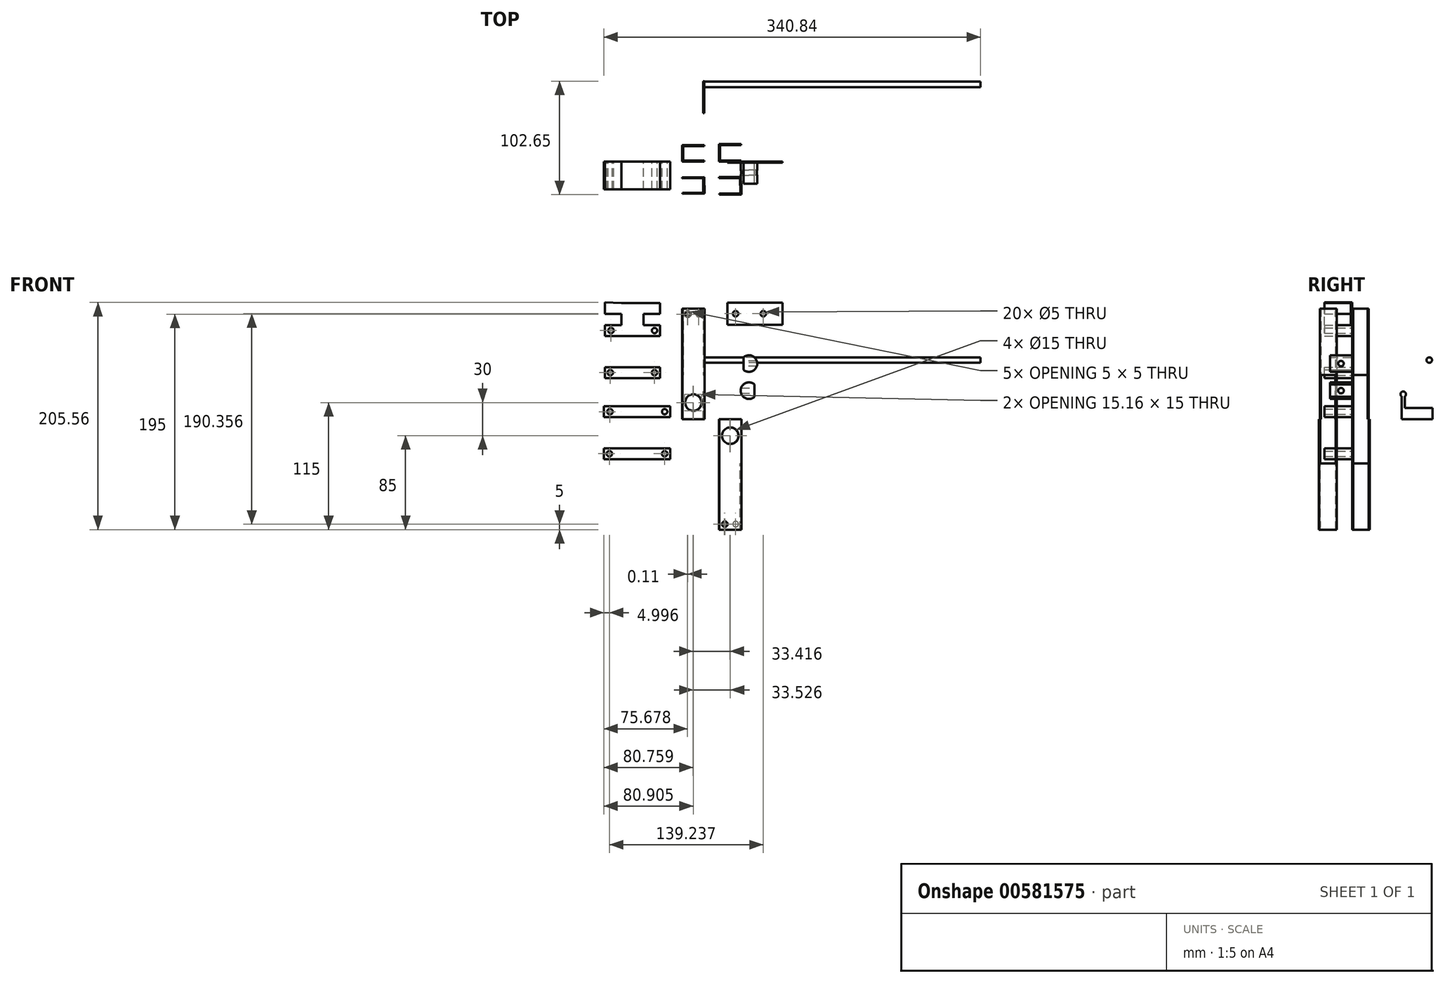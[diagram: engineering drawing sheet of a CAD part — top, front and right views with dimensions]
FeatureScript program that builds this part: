
annotation { "Feature Type Name" : "Feature", "Feature Type Description" : "" }
export const myFeature = defineFeature(function(context is Context, id is Id, definition is map)
    precondition{}
    {
        {
            var Q0;
            Q0=qCreatedBy(makeId("Top.planeOp"),FACE);
            var sketch = newSketch(context, id + "F0", { "sketchPlane" : qUnion([Q0])});
            skLineSegment(sketch, "E0", {"start": v(0, 15) * mm, "end": v(-20, 15) * mm});
            skLineSegment(sketch, "E1", {"start": v(-20, 15) * mm, "end": v(-20, 0) * mm});
            skLineSegment(sketch, "E2", {"start": v(-20, 0) * mm, "end": v(0, 0) * mm});
            skLineSegment(sketch, "E3", {"start": v(0, 0) * mm, "end": v(0, 1) * mm});
            skLineSegment(sketch, "E4", {"start": v(0, 1) * mm, "end": v(-19, 1) * mm});
            skLineSegment(sketch, "E5", {"start": v(-19, 1) * mm, "end": v(-19, 14) * mm});
            skLineSegment(sketch, "E6", {"start": v(-19, 14) * mm, "end": v(0, 14) * mm});
            skLineSegment(sketch, "E7", {"start": v(0, 14) * mm, "end": v(0, 15) * mm});
            skLineSegment(sketch, "E8", {"start": v(33.42, 1) * mm, "end": v(14.42, 1) * mm});
            skLineSegment(sketch, "E9", {"start": v(14.42, 1) * mm, "end": v(14.42, 15) * mm});
            skLineSegment(sketch, "E10", {"start": v(14.42, 15) * mm, "end": v(33.42, 15) * mm});
            skLineSegment(sketch, "E11", {"start": v(33.42, 15) * mm, "end": v(33.42, 16) * mm});
            skLineSegment(sketch, "E12", {"start": v(33.42, 16) * mm, "end": v(13.42, 16) * mm});
            skLineSegment(sketch, "E13", {"start": v(13.42, 16) * mm, "end": v(13.42, 0) * mm});
            skLineSegment(sketch, "E14", {"start": v(13.42, 0) * mm, "end": v(33.42, 0) * mm});
            skLineSegment(sketch, "E15", {"start": v(33.42, 0) * mm, "end": v(33.42, 1) * mm});
            skLineSegment(sketch, "E16", {"start": v(-36.62, -7.13) * mm, "end": v(38.64, -6.85) * mm, "construction": true});
            skLineSegment(sketch, "E17.MirrorCS", {"start": v(-19, 16) * mm, "end": v(0, 16) * mm});
            skLineSegment(sketch, "E18.MirrorCS", {"start": v(-19.95, -14.13) * mm, "end": v(0.05, -13.99) * mm});
            skLineSegment(sketch, "E19.MirrorCS", {"start": v(0.16, -28.99) * mm, "end": v(-19.84, -29.13) * mm});
            skLineSegment(sketch, "E20.MirrorCS", {"start": v(13.47, -13.89) * mm, "end": v(33.47, -13.74) * mm});
            skLineSegment(sketch, "E21.MirrorCS", {"start": v(33.58, -29.74) * mm, "end": v(13.58, -29.89) * mm});
            skLineSegment(sketch, "E22", {"start": v(13.47, -13.89) * mm, "end": v(13.47, -14.89) * mm});
            skLineSegment(sketch, "E23", {"start": v(13.47, -14.89) * mm, "end": v(32.47, -14.75) * mm});
            skLineSegment(sketch, "E24", {"start": v(32.58, -28.75) * mm, "end": v(13.58, -28.89) * mm});
            skLineSegment(sketch, "E25", {"start": v(13.58, -28.89) * mm, "end": v(13.58, -29.89) * mm});
            skLineSegment(sketch, "E26", {"start": v(32.58, -28.75) * mm, "end": v(32.47, -14.75) * mm});
            skLineSegment(sketch, "E27", {"start": v(33.47, -13.74) * mm, "end": v(33.58, -29.74) * mm});
            skLineSegment(sketch, "E28", {"start": v(0.05, -13.99) * mm, "end": v(0.16, -28.99) * mm});
            skLineSegment(sketch, "E29", {"start": v(-19.95, -14.13) * mm, "end": v(-19.94, -15.13) * mm});
            skLineSegment(sketch, "E30", {"start": v(-19.94, -15.13) * mm, "end": v(-0.94, -15) * mm});
            skLineSegment(sketch, "E31", {"start": v(-0.94, -15) * mm, "end": v(-0.85, -28) * mm});
            skLineSegment(sketch, "E32", {"start": v(-0.85, -28) * mm, "end": v(-19.84, -28.13) * mm});
            skLineSegment(sketch, "E33", {"start": v(-19.84, -29.13) * mm, "end": v(-19.84, -28.13) * mm});
            skSolve(sketch);
        }
        {
            var Q0;
            Q0=makeQuery(id+"F0.imprint","IMPRINT",FACE,{"disambiguationData":[TD([[makeQuery(id+"F0.imprint","IMPRINT",EDGE,{"derivedFrom":sQuery(id+"F0.wireOp",EDGE,"E0")}),1.0]])]});
            var Q1;
            Q1=makeQuery(id+"F0.imprint","IMPRINT",FACE,{"disambiguationData":[TD([[makeQuery(id+"F0.imprint","IMPRINT",EDGE,{"derivedFrom":sQuery(id+"F0.wireOp",EDGE,"E19.MirrorCS")}),-1.0]])]});
            extrude(context, id + "F1", {"entities" : qUnion([Q0, Q1]), "depth" : 100 * mm, "offsetDistance" : 25 * mm});
        }
        {
            var Q0;
            Q0=makeQuery(id+"F1.opExtrude","SWEPT_FACE",FACE,{"disambiguationData":[OSD([sQuery(id+"F0.wireOp",EDGE,"E2")])]});
            var sketch = newSketch(context, id + "F2", { "sketchPlane" : qUnion([Q0])});
            skCircle(sketch, "E34", {"center": v(-10, 15) * mm, "radius": 7.5 * mm});
            skPoint(sketch, "E34.centerSnap0", {"position": v(-10, 0) * mm});
            skCircle(sketch, "E35", {"center": v(-5, 95) * mm, "radius": 2.5 * mm});
            skSolve(sketch);
        }
        {
            var Q0;
            Q0=makeQuery(id+"F2.imprint","IMPRINT",FACE,{"disambiguationData":[TD([[makeQuery(id+"F2.imprint","IMPRINT",EDGE,{"derivedFrom":sQuery(id+"F2.wireOp",EDGE,"E34")}),1.0]])]});
            var Q1;
            Q1=makeQuery(id+"F2.imprint","IMPRINT",FACE,{"disambiguationData":[TD([[makeQuery(id+"F2.imprint","IMPRINT",EDGE,{"derivedFrom":sQuery(id+"F2.wireOp",EDGE,"E35")}),1.0]])]});
            extrude(context, id + "F3", {"entities" : qUnion([Q0, Q1]), "operationType" : NewBodyOperationType.REMOVE, "endBound" : BoundingType.THROUGH_ALL, "oppositeDirection" : true, "depth" : 25 * mm, "offsetDistance" : 25 * mm});
        }
        {
            var Q0;
            Q0=makeQuery(id+"F1.opExtrude","SWEPT_FACE",FACE,{"disambiguationData":[OSD([sQuery(id+"F0.wireOp",EDGE,"E1")])]});
            var sketch = newSketch(context, id + "F4", { "sketchPlane" : qUnion([Q0])});
            skPoint(sketch, "E36.centerSnap0", {"position": v(-7.5, 0) * mm});
            skLineSegment(sketch, "E37", {"start": v(-14, 0) * mm, "end": v(-14, 40) * mm});
            skLineSegment(sketch, "E38", {"start": v(-14, 40) * mm, "end": v(-1, 40) * mm});
            skLineSegment(sketch, "E39", {"start": v(-1, 40) * mm, "end": v(-1, 0) * mm});
            skSolve(sketch);
        }
        {
            var Q0;
            {var subQ0=sQuery(id+"F4.wireOp",EDGE,"E37");Q0=makeQuery(id+"F4.imprint","IMPRINT",FACE,{"disambiguationData":[TD([[makeQuery(id+"F4.imprint","IMPRINT",EDGE,{"derivedFrom":subQ0}),-1.0]])]});}
            extrude(context, id + "F5", {"entities" : qUnion([Q0]), "operationType" : NewBodyOperationType.REMOVE, "endBound" : BoundingType.THROUGH_ALL, "oppositeDirection" : true, "depth" : 25 * mm, "offsetDistance" : 25 * mm});
        }
        {
            var Q0;
            Q0=makeQuery(id+"F0.imprint","IMPRINT",FACE,{"disambiguationData":[TD([[makeQuery(id+"F0.imprint","IMPRINT",EDGE,{"derivedFrom":sQuery(id+"F0.wireOp",EDGE,"E8")}),1.0]])]});
            var Q1;
            Q1=makeQuery(id+"F0.imprint","IMPRINT",FACE,{"disambiguationData":[TD([[makeQuery(id+"F0.imprint","IMPRINT",EDGE,{"derivedFrom":sQuery(id+"F0.wireOp",EDGE,"E20.MirrorCS")}),-1.0]])]});
            extrude(context, id + "F6", {"entities" : qUnion([Q0, Q1]), "oppositeDirection" : true, "depth" : 100 * mm, "offsetDistance" : 25 * mm});
        }
        {
            var Q0;
            Q0=makeQuery(id+"F6.opExtrude","SWEPT_FACE",FACE,{"disambiguationData":[OSD([sQuery(id+"F0.wireOp",EDGE,"E14")])]});
            var sketch = newSketch(context, id + "F7", { "sketchPlane" : qUnion([Q0])});
            skCircle(sketch, "E40", {"center": v(23.42, -15) * mm, "radius": 7.5 * mm});
            skPoint(sketch, "E40.centerSnap0", {"position": v(23.42, 0) * mm});
            skCircle(sketch, "E41", {"center": v(28.42, -95) * mm, "radius": 2.5 * mm});
            skSolve(sketch);
        }
        {
            var Q0;
            Q0=makeQuery(id+"F7.imprint","IMPRINT",FACE,{"disambiguationData":[TD([[makeQuery(id+"F7.imprint","IMPRINT",EDGE,{"derivedFrom":sQuery(id+"F7.wireOp",EDGE,"E40")}),1.0]])]});
            var Q1;
            Q1=makeQuery(id+"F7.imprint","IMPRINT",FACE,{"disambiguationData":[TD([[makeQuery(id+"F7.imprint","IMPRINT",EDGE,{"derivedFrom":sQuery(id+"F7.wireOp",EDGE,"E41")}),1.0]])]});
            extrude(context, id + "F8", {"entities" : qUnion([Q0, Q1]), "operationType" : NewBodyOperationType.REMOVE, "endBound" : BoundingType.THROUGH_ALL, "oppositeDirection" : true, "depth" : 25 * mm, "offsetDistance" : 25 * mm});
        }
        {
            var Q0;
            Q0=makeQuery(id+"F6.opExtrude","SWEPT_FACE",FACE,{"disambiguationData":[OSD([sQuery(id+"F0.wireOp",EDGE,"E13")])]});
            var sketch = newSketch(context, id + "F9", { "sketchPlane" : qUnion([Q0])});
            skLineSegment(sketch, "E42", {"start": v(-15, 0) * mm, "end": v(-15, -40) * mm});
            skLineSegment(sketch, "E43", {"start": v(-15, -40) * mm, "end": v(-1, -40) * mm});
            skLineSegment(sketch, "E44", {"start": v(-1, -40) * mm, "end": v(-1, 0) * mm});
            skSolve(sketch);
        }
        {
            var Q0;
            {var subQ0=sQuery(id+"F9.wireOp",EDGE,"E42");Q0=makeQuery(id+"F9.imprint","IMPRINT",FACE,{"disambiguationData":[TD([[makeQuery(id+"F9.imprint","IMPRINT",EDGE,{"derivedFrom":subQ0}),1.0]])]});}
            extrude(context, id + "F10", {"entities" : qUnion([Q0]), "operationType" : NewBodyOperationType.REMOVE, "endBound" : BoundingType.THROUGH_ALL, "oppositeDirection" : true, "depth" : 25 * mm, "offsetDistance" : 25 * mm});
        }
        {
            var Q0;
            Q0=qCreatedBy(makeId("Front.planeOp"),FACE);
            var sketch = newSketch(context, id + "F11", { "sketchPlane" : qUnion([Q0])});
            skLineSegment(sketch, "E45.bottom", {"start": v(20.9, 105.36) * mm, "end": v(70.9, 105.36) * mm});
            skLineSegment(sketch, "E45.top", {"start": v(20.9, 85.36) * mm, "end": v(70.9, 85.36) * mm});
            skLineSegment(sketch, "E45.left", {"start": v(20.9, 105.36) * mm, "end": v(20.9, 85.36) * mm});
            skLineSegment(sketch, "E45.right", {"start": v(70.9, 105.36) * mm, "end": v(70.9, 85.36) * mm});
            skCircle(sketch, "E46", {"center": v(28.4, 95.36) * mm, "radius": 2.5 * mm});
            skPoint(sketch, "E46.centerSnap0", {"position": v(20.9, 95.36) * mm});
            skCircle(sketch, "E47.MirrorC", {"center": v(53.4, 95.36) * mm, "radius": 2.5 * mm});
            skSolve(sketch);
        }
        {
            var Q0;
            Q0=makeQuery(id+"F11.imprint","IMPRINT",FACE,{"disambiguationData":[TD([[makeQuery(id+"F11.imprint","IMPRINT",EDGE,{"derivedFrom":sQuery(id+"F11.wireOp",EDGE,"E45.bottom")}),-1.0]])]});
            extrude(context, id + "F12", {"entities" : qUnion([Q0]), "depth" : 1 * mm, "offsetDistance" : 25 * mm});
        }
        {
            var Q0;
            Q0=makeQuery(id+"F1.opExtrude","SWEPT_FACE",FACE,{"disambiguationData":[OSD([sQuery(id+"F0.wireOp",EDGE,"E19.MirrorCS")])]});
            var sketch = newSketch(context, id + "F13", { "sketchPlane" : qUnion([Q0])});
            skCircle(sketch, "E48", {"center": v(-15.05, 95) * mm, "radius": 2.5 * mm});
            skCircle(sketch, "E49", {"center": v(-10.05, 15) * mm, "radius": 7.5 * mm});
            skPoint(sketch, "E49.centerSnap0", {"position": v(-10.05, 0) * mm});
            skSolve(sketch);
        }
        {
            var Q0;
            Q0=makeQuery(id+"F13.imprint","IMPRINT",FACE,{"disambiguationData":[TD([[makeQuery(id+"F13.imprint","IMPRINT",EDGE,{"derivedFrom":sQuery(id+"F13.wireOp",EDGE,"E48")}),1.0]])]});
            var Q1;
            Q1=makeQuery(id+"F13.imprint","IMPRINT",FACE,{"disambiguationData":[TD([[makeQuery(id+"F13.imprint","IMPRINT",EDGE,{"derivedFrom":sQuery(id+"F13.wireOp",EDGE,"E49")}),1.0]])]});
            extrude(context, id + "F14", {"entities" : qUnion([Q0, Q1]), "operationType" : NewBodyOperationType.REMOVE, "endBound" : BoundingType.THROUGH_ALL, "oppositeDirection" : true, "depth" : 25 * mm, "offsetDistance" : 25 * mm});
        }
        {
            var Q0;
            Q0=makeQuery(id+"F6.opExtrude","SWEPT_FACE",FACE,{"disambiguationData":[OSD([sQuery(id+"F0.wireOp",EDGE,"E21.MirrorCS")])]});
            var sketch = newSketch(context, id + "F15", { "sketchPlane" : qUnion([Q0])});
            skCircle(sketch, "E50", {"center": v(23.36, -15) * mm, "radius": 7.5 * mm});
            skPoint(sketch, "E50.centerSnap0", {"position": v(23.36, 0) * mm});
            skCircle(sketch, "E51", {"center": v(18.36, -95) * mm, "radius": 2.5 * mm});
            skSolve(sketch);
        }
        {
            var Q0;
            Q0 = qSketchRegion(id + "F15", true);
            extrude(context, id + "F16", {"entities" : qUnion([Q0]), "operationType" : NewBodyOperationType.REMOVE, "endBound" : BoundingType.THROUGH_ALL, "oppositeDirection" : true, "depth" : 25 * mm, "offsetDistance" : 25 * mm});
        }
        {
            var Q0;
            Q0=makeQuery(id+"F6.opExtrude","SWEPT_FACE",FACE,{"disambiguationData":[OSD([sQuery(id+"F0.wireOp",EDGE,"E27")])]});
            var sketch = newSketch(context, id + "F17", { "sketchPlane" : qUnion([Q0])});
            skLineSegment(sketch, "E52", {"start": v(-14.99, -40) * mm, "end": v(-28.99, -40) * mm});
            skLineSegment(sketch, "E53", {"start": v(-28.99, -40) * mm, "end": v(-28.99, 0) * mm});
            skLineSegment(sketch, "E54", {"start": v(-14.99, -40) * mm, "end": v(-14.99, 0) * mm});
            skSolve(sketch);
        }
        {
            var Q0;
            Q0=makeQuery(id+"F17.imprint","IMPRINT",FACE,{"disambiguationData":[TD([[makeQuery(id+"F17.imprint","IMPRINT",EDGE,{"derivedFrom":sQuery(id+"F17.wireOp",EDGE,"E52")}),-1.0]])]});
            extrude(context, id + "F18", {"entities" : qUnion([Q0]), "operationType" : NewBodyOperationType.REMOVE, "endBound" : BoundingType.THROUGH_ALL, "oppositeDirection" : true, "depth" : 25 * mm, "offsetDistance" : 25 * mm});
        }
        {
            var Q0;
            Q0=makeQuery(id+"F1.opExtrude","SWEPT_FACE",FACE,{"disambiguationData":[OSD([sQuery(id+"F0.wireOp",EDGE,"E28")])]});
            var sketch = newSketch(context, id + "F19", { "sketchPlane" : qUnion([Q0])});
            skLineSegment(sketch, "E55", {"start": v(-14.99, 0) * mm, "end": v(-14.99, 40) * mm});
            skLineSegment(sketch, "E56", {"start": v(-14.99, 40) * mm, "end": v(-27.99, 40) * mm});
            skLineSegment(sketch, "E57", {"start": v(-27.99, 40) * mm, "end": v(-27.99, 0) * mm});
            skSolve(sketch);
        }
        {
            var Q0;
            {var subQ0=sQuery(id+"F19.wireOp",EDGE,"E55");Q0=makeQuery(id+"F19.imprint","IMPRINT",FACE,{"disambiguationData":[TD([[makeQuery(id+"F19.imprint","IMPRINT",EDGE,{"derivedFrom":subQ0}),1.0]])]});}
            extrude(context, id + "F20", {"entities" : qUnion([Q0]), "operationType" : NewBodyOperationType.REMOVE, "oppositeDirection" : true, "depth" : 25 * mm, "offsetDistance" : 25 * mm});
        }
        {
            var Q0;
            Q0=qCreatedBy(makeId("Front.planeOp"),FACE);
            var sketch = newSketch(context, id + "F21", { "sketchPlane" : qUnion([Q0])});
            skArc(sketch, "E58", {"start": v(35.49, 44.6) * mm, "mid": v(47.93, 50.24) * mm, "end": v(35.49, 55.88) * mm});
            skArc(sketch, "E59", {"start": v(45.38, 31.4) * mm, "mid": v(32.93, 25.77) * mm, "end": v(45.38, 20.13) * mm});
            skLineSegment(sketch, "E60", {"start": v(35.49, 55.88) * mm, "end": v(35.49, 44.6) * mm});
            skLineSegment(sketch, "E61.trimOffspring", {"start": v(45.38, 31.4) * mm, "end": v(45.38, 20.13) * mm});
            skPoint(sketch, "E62.orphan", {"position": v(40.43, 57.74) * mm});
            skSolve(sketch);
        }
        {
            var Q0;
            Q0=makeQuery(id+"F21.imprint","IMPRINT",FACE,{"disambiguationData":[TD([[makeQuery(id+"F21.imprint","IMPRINT",EDGE,{"derivedFrom":sQuery(id+"F21.wireOp",EDGE,"E58")}),1.0]])]});
            var Q1;
            Q1=makeQuery(id+"F21.imprint","IMPRINT",FACE,{"disambiguationData":[TD([[makeQuery(id+"F21.imprint","IMPRINT",EDGE,{"derivedFrom":sQuery(id+"F21.wireOp",EDGE,"E59")}),1.0]])]});
            extrude(context, id + "F22", {"entities" : qUnion([Q0, Q1]), "depth" : 20 * mm, "offsetDistance" : 25 * mm});
        }
        {
            var Q0;
            Q0=qCreatedBy(makeId("Right.planeOp"),FACE);
            var sketch = newSketch(context, id + "F23", { "sketchPlane" : qUnion([Q0])});
            skCircle(sketch, "E63", {"center": v(69.88, 53.43) * mm, "radius": 2.5 * mm});
            skSolve(sketch);
        }
        {
            var Q0;
            Q0=makeQuery(id+"F23.imprint","IMPRINT",FACE,{"disambiguationData":[TD([[makeQuery(id+"F23.imprint","IMPRINT",EDGE,{"derivedFrom":sQuery(id+"F23.wireOp",EDGE,"E63")}),1.0]])]});
            extrude(context, id + "F24", {"entities" : qUnion([Q0]), "depth" : 250 * mm, "offsetDistance" : 25 * mm});
        }
        {
            var Q0;
            Q0=qCreatedBy(makeId("Front.planeOp"),FACE);
            var sketch = newSketch(context, id + "F25", { "sketchPlane" : qUnion([Q0])});
            skLineSegment(sketch, "E64.top", {"start": v(-89.95, 75.12) * mm, "end": v(-39.95, 75.12) * mm});
            skLineSegment(sketch, "E64.left", {"start": v(-89.95, 85.12) * mm, "end": v(-89.95, 75.12) * mm});
            skLineSegment(sketch, "E64.right", {"start": v(-39.95, 85.12) * mm, "end": v(-39.95, 75.12) * mm});
            skCircle(sketch, "E65", {"center": v(-84.38, 80.12) * mm, "radius": 2.5 * mm});
            skPoint(sketch, "E65.centerSnap0", {"position": v(-89.95, 80.12) * mm});
            skCircle(sketch, "E66", {"center": v(-44.95, 80.12) * mm, "radius": 2.41 * mm});
            skPoint(sketch, "E66.centerSnap0", {"position": v(-39.95, 80.12) * mm});
            skLineSegment(sketch, "E67.MirrorCS", {"start": v(-89.95, 47.06) * mm, "end": v(-39.95, 47.06) * mm});
            skLineSegment(sketch, "E68.MirrorCS", {"start": v(-89.95, 37.06) * mm, "end": v(-89.95, 47.06) * mm});
            skLineSegment(sketch, "E69.MirrorCS", {"start": v(-89.95, 37.06) * mm, "end": v(-39.95, 37.06) * mm});
            skLineSegment(sketch, "E70.MirrorCS", {"start": v(-39.95, 37.06) * mm, "end": v(-39.95, 47.06) * mm});
            skCircle(sketch, "E71", {"center": v(-84.95, 42.06) * mm, "radius": 2.5 * mm});
            skPoint(sketch, "E71.centerSnap0", {"position": v(-89.95, 42.06) * mm});
            skCircle(sketch, "E72", {"center": v(-44.95, 42.06) * mm, "radius": 2.5 * mm});
            skPoint(sketch, "E72.centerSnap0", {"position": v(-39.95, 42.06) * mm});
            skLineSegment(sketch, "E73.bottom", {"start": v(-90.84, 11.74) * mm, "end": v(-30.84, 11.74) * mm});
            skLineSegment(sketch, "E73.top", {"start": v(-90.84, 1.74) * mm, "end": v(-30.84, 1.74) * mm});
            skLineSegment(sketch, "E73.left", {"start": v(-90.84, 11.74) * mm, "end": v(-90.84, 1.74) * mm});
            skLineSegment(sketch, "E73.right", {"start": v(-30.84, 11.74) * mm, "end": v(-30.84, 1.74) * mm});
            skCircle(sketch, "E74", {"center": v(-85.27, 6.74) * mm, "radius": 2.5 * mm});
            skPoint(sketch, "E74.centerSnap0", {"position": v(-90.84, 6.74) * mm});
            skCircle(sketch, "E75", {"center": v(-35.84, 6.74) * mm, "radius": 2.41 * mm});
            skPoint(sketch, "E75.centerSnap0", {"position": v(-30.84, 6.74) * mm});
            skLineSegment(sketch, "E76.MirrorCS", {"start": v(-90.84, -36.32) * mm, "end": v(-90.84, -26.32) * mm});
            skLineSegment(sketch, "E77.MirrorCS", {"start": v(-30.84, -36.32) * mm, "end": v(-30.84, -26.32) * mm});
            skCircle(sketch, "E78", {"center": v(-85.84, -31.32) * mm, "radius": 2.5 * mm});
            skPoint(sketch, "E78.centerSnap0", {"position": v(-90.84, -31.32) * mm});
            skCircle(sketch, "E79", {"center": v(-35.84, -31.32) * mm, "radius": 2.5 * mm});
            skPoint(sketch, "E79.centerSnap0", {"position": v(-30.84, -31.32) * mm});
            skLineSegment(sketch, "E80", {"start": v(-90.84, -26.32) * mm, "end": v(-30.84, -26.32) * mm});
            skLineSegment(sketch, "E81", {"start": v(-90.84, -36.32) * mm, "end": v(-30.84, -36.32) * mm});
            skLineSegment(sketch, "E82", {"start": v(-74.95, 85.12) * mm, "end": v(-74.95, 95.12) * mm});
            skLineSegment(sketch, "E83", {"start": v(-74.95, 105.12) * mm, "end": v(-64.95, 105.12) * mm});
            skLineSegment(sketch, "E84.MirrorCS", {"start": v(-54.95, 85.12) * mm, "end": v(-54.95, 95.12) * mm});
            skLineSegment(sketch, "E85.MirrorCS", {"start": v(-54.95, 105.12) * mm, "end": v(-64.95, 105.12) * mm});
            skLineSegment(sketch, "E86.MirrorCS", {"start": v(-89.95, 135.12) * mm, "end": v(-39.95, 135.12) * mm});
            skLineSegment(sketch, "E87.MirrorCS", {"start": v(-89.95, 85.12) * mm, "end": v(-74.95, 85.12) * mm});
            skLineSegment(sketch, "E88", {"start": v(-89.95, 95.12) * mm, "end": v(-89.95, 105.56) * mm});
            skLineSegment(sketch, "E89", {"start": v(-89.95, 105.56) * mm, "end": v(-74.95, 105.12) * mm});
            skLineSegment(sketch, "E90", {"start": v(-54.95, 105.12) * mm, "end": v(-39.95, 105.12) * mm});
            skLineSegment(sketch, "E91", {"start": v(-39.95, 105.12) * mm, "end": v(-39.95, 95.12) * mm});
            skLineSegment(sketch, "E92.trimOffspring", {"start": v(-54.95, 95.12) * mm, "end": v(-39.95, 95.12) * mm});
            skLineSegment(sketch, "E93", {"start": v(-74.95, 95.12) * mm, "end": v(-89.95, 95.12) * mm});
            skLineSegment(sketch, "E94.trimOffspring", {"start": v(-54.95, 85.12) * mm, "end": v(-39.95, 85.12) * mm});
            skPoint(sketch, "E95.end.orphan", {"position": v(-64.95, 75.12) * mm});
            skPoint(sketch, "E95.start.orphan", {"position": v(-64.95, 85.12) * mm});
            skSolve(sketch);
        }
        {
            var Q0;
            Q0=makeQuery(id+"F25.imprint","IMPRINT",FACE,{"disambiguationData":[TD([[makeQuery(id+"F25.imprint","IMPRINT",EDGE,{"derivedFrom":sQuery(id+"F25.wireOp",EDGE,"E64.bottom")}),-1.0]])]});
            var Q1;
            {var subQ2=sQuery(id+"F25.wireOp",EDGE,"E68.MirrorCS");Q1=makeQuery(id+"F25.imprint","IMPRINT",FACE,{"disambiguationData":[TD([[makeQuery(id+"F25.imprint","IMPRINT",EDGE,{"derivedFrom":subQ2}),-1.0]])]});}
            var Q2;
            Q2=makeQuery(id+"F25.imprint","IMPRINT",FACE,{"disambiguationData":[TD([[makeQuery(id+"F25.imprint","IMPRINT",EDGE,{"derivedFrom":sQuery(id+"F25.wireOp",EDGE,"E64.top")}),1.0]])]});
            extrude(context, id + "F26", {"entities" : qUnion([Q0, Q1, Q2]), "depth" : 25 * mm, "offsetDistance" : 25 * mm});
        }
        {
            var Q0;
            Q0=makeQuery(id+"F25.imprint","IMPRINT",FACE,{"disambiguationData":[TD([[makeQuery(id+"F25.imprint","IMPRINT",EDGE,{"derivedFrom":sQuery(id+"F25.wireOp",EDGE,"E76.MirrorCS")}),-1.0]])]});
            var Q1;
            Q1=makeQuery(id+"F25.imprint","IMPRINT",FACE,{"disambiguationData":[TD([[makeQuery(id+"F25.imprint","IMPRINT",EDGE,{"derivedFrom":sQuery(id+"F25.wireOp",EDGE,"E73.bottom")}),-1.0]])]});
            extrude(context, id + "F27", {"entities" : qUnion([Q0, Q1]), "depth" : 25 * mm, "offsetDistance" : 25 * mm});
        }
        {
            var Q0;
            Q0=makeQuery(id+"F22.opExtrude","SWEPT_FACE",FACE,{"disambiguationData":[OSD([sQuery(id+"F21.wireOp",EDGE,"E61.trimOffspring")])]});
            var sketch = newSketch(context, id + "F28", { "sketchPlane" : qUnion([Q0])});
            skCircle(sketch, "E96", {"center": v(-10, 25.77) * mm, "radius": 2.5 * mm});
            skPoint(sketch, "E96.centerSnap0", {"position": v(-20, 25.77) * mm});
            skPoint(sketch, "E96.centerSnap1", {"position": v(-10, 31.4) * mm});
            skSolve(sketch);
        }
        {
            var Q0;
            Q0=makeQuery(id+"F28.imprint","IMPRINT",FACE,{"disambiguationData":[TD([[makeQuery(id+"F28.imprint","IMPRINT",EDGE,{"derivedFrom":sQuery(id+"F28.wireOp",EDGE,"E96")}),1.0]])]});
            extrude(context, id + "F29", {"entities" : qUnion([Q0]), "operationType" : NewBodyOperationType.REMOVE, "endBound" : BoundingType.THROUGH_ALL, "oppositeDirection" : true, "depth" : 25 * mm, "offsetDistance" : 25 * mm});
        }
        {
            var Q0;
            Q0=makeQuery(id+"F22.opExtrude","SWEPT_FACE",FACE,{"disambiguationData":[OSD([sQuery(id+"F21.wireOp",EDGE,"E60")])]});
            var sketch = newSketch(context, id + "F30", { "sketchPlane" : qUnion([Q0])});
            skCircle(sketch, "E97", {"center": v(10, 50.24) * mm, "radius": 2.5 * mm});
            skPoint(sketch, "E97.centerSnap0", {"position": v(10, 44.6) * mm});
            skPoint(sketch, "E97.centerSnap1", {"position": v(0, 50.24) * mm});
            skSolve(sketch);
        }
        {
            var Q0;
            Q0=makeQuery(id+"F30.imprint","IMPRINT",FACE,{"disambiguationData":[TD([[makeQuery(id+"F30.imprint","IMPRINT",EDGE,{"derivedFrom":sQuery(id+"F30.wireOp",EDGE,"E97")}),1.0]])]});
            extrude(context, id + "F31", {"entities" : qUnion([Q0]), "operationType" : NewBodyOperationType.REMOVE, "endBound" : BoundingType.THROUGH_ALL, "oppositeDirection" : true, "depth" : 25 * mm, "offsetDistance" : 25 * mm});
        }
        {
            var Q0;
            Q0=qCreatedBy(makeId("Right.planeOp"),FACE);
            var sketch = newSketch(context, id + "F32", { "sketchPlane" : qUnion([Q0])});
            skArc(sketch, "E98", {"start": v(47.76, 20.47) * mm, "mid": v(46.3, 25) * mm, "end": v(44.85, 20.47) * mm});
            skLineSegment(sketch, "E99", {"start": v(47.76, 8.68) * mm, "end": v(47.76, 20.47) * mm});
            skLineSegment(sketch, "E100.MirrorCS", {"start": v(44.85, 8.68) * mm, "end": v(44.85, 20.47) * mm});
            skLineSegment(sketch, "E101", {"start": v(37.92, 27.31) * mm, "end": v(57.96, 27.31) * mm, "construction": true});
            skLineSegment(sketch, "E102", {"start": v(44.85, 8.68) * mm, "end": v(44.85, 0) * mm});
            skLineSegment(sketch, "E103", {"start": v(44.85, 0) * mm, "end": v(47.76, 0) * mm});
            skLineSegment(sketch, "E104", {"start": v(47.76, 0) * mm, "end": v(47.76, 8.68) * mm});
            skArc(sketch, "E105.MirrorCS", {"start": v(47.76, 34.16) * mm, "mid": v(46.3, 29.63) * mm, "end": v(44.85, 34.16) * mm});
            skLineSegment(sketch, "E106.MirrorCS", {"start": v(44.85, 45.94) * mm, "end": v(44.85, 34.16) * mm});
            skLineSegment(sketch, "E107.MirrorCS", {"start": v(47.76, 45.94) * mm, "end": v(47.76, 34.16) * mm});
            skLineSegment(sketch, "E108.MirrorCS", {"start": v(44.85, 45.94) * mm, "end": v(44.85, 54.62) * mm});
            skLineSegment(sketch, "E109.MirrorCS", {"start": v(47.76, 54.62) * mm, "end": v(47.76, 45.94) * mm});
            skLineSegment(sketch, "E110.MirrorCS", {"start": v(44.85, 54.62) * mm, "end": v(47.76, 54.62) * mm});
            skSolve(sketch);
        }
        {
            var Q0;
            Q0=makeQuery(id+"F32.imprint","IMPRINT",FACE,{"disambiguationData":[TD([[makeQuery(id+"F32.imprint","IMPRINT",EDGE,{"derivedFrom":sQuery(id+"F32.wireOp",EDGE,"E98")}),1.0]])]});
            var Q1;
            Q1=makeQuery(id+"F32.imprint","IMPRINT",FACE,{"disambiguationData":[TD([[makeQuery(id+"F32.imprint","IMPRINT",EDGE,{"derivedFrom":sQuery(id+"F32.wireOp",EDGE,"E105.MirrorCS")}),-1.0]])]});
            extrude(context, id + "F33", {"entities" : qUnion([Q0, Q1]), "oppositeDirection" : true, "depth" : 1 * mm, "offsetDistance" : 25 * mm});
        }
        {
            var Q0;
            Q0=makeQuery(id+"F33.opExtrude","SWEPT_FACE",FACE,{"disambiguationData":[OSD([sQuery(id+"F32.wireOp",EDGE,"E99"),sQuery(id+"F32.wireOp",EDGE,"E104")])]});
            var sketch = newSketch(context, id + "F34", { "sketchPlane" : qUnion([Q0])});
            skLineSegment(sketch, "E111", {"start": v(0, 10) * mm, "end": v(1, 10) * mm});
            skLineSegment(sketch, "E112", {"start": v(0.98, 44.62) * mm, "end": v(0, 44.62) * mm});
            skSolve(sketch);
        }
        {
            var Q0;
            {var subQ0=sQuery(id+"F34.wireOp",EDGE,"E111");Q0=makeQuery(id+"F34.imprint","IMPRINT",FACE,{"disambiguationData":[TD([[makeQuery(id+"F34.imprint","IMPRINT",EDGE,{"derivedFrom":subQ0}),-1.0]])]});}
            extrude(context, id + "F35", {"entities" : qUnion([Q0]), "operationType" : NewBodyOperationType.ADD, "depth" : 25 * mm, "offsetDistance" : 25 * mm});
        }
    });
